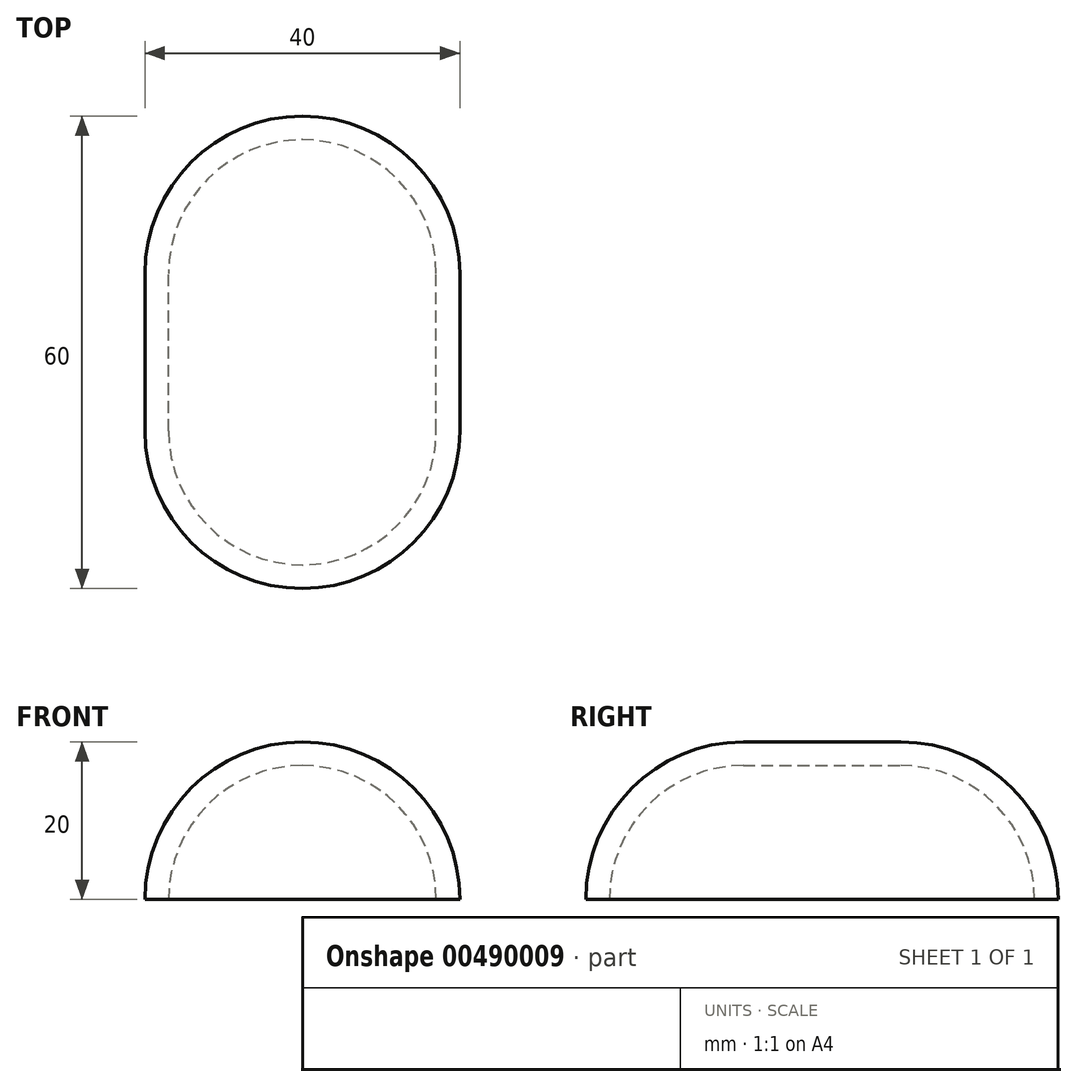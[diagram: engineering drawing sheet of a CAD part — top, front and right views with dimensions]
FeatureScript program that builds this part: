
annotation { "Feature Type Name" : "Feature", "Feature Type Description" : "" }
export const myFeature = defineFeature(function(context is Context, id is Id, definition is map)
    precondition{}
    {
        {
            var Q0;
            Q0=qCreatedBy(makeId("Top.planeOp"),FACE);
            var sketch = newSketch(context, id + "F0", { "sketchPlane" : qUnion([Q0])});
            skLineSegment(sketch, "E0.bottom", {"start": v(0, -30) * mm, "end": v(0, -30) * mm});
            skLineSegment(sketch, "E0.top", {"start": v(0, 30) * mm, "end": v(0, 30) * mm});
            skLineSegment(sketch, "E0.left", {"start": v(20, -10) * mm, "end": v(20, 10) * mm});
            skLineSegment(sketch, "E0.right", {"start": v(-20, -10) * mm, "end": v(-20, 10) * mm});
            skPoint(sketch, "E0.middle", {"position": v(0, 0) * mm});
            skPoint(sketch, "E1.visualSharp", {"position": v(-20, 30) * mm});
            skArc(sketch, "E1.filletArc", {"start": v(0, 30) * mm, "mid": v(-14.14, 24.14) * mm, "end": v(-20, 10) * mm});
            skPoint(sketch, "E2.visualSharp", {"position": v(20, 30) * mm});
            skArc(sketch, "E2.filletArc", {"start": v(20, 10) * mm, "mid": v(14.14, 24.14) * mm, "end": v(0, 30) * mm});
            skPoint(sketch, "E3.visualSharp", {"position": v(20, -30) * mm});
            skArc(sketch, "E3.filletArc", {"start": v(0, -30) * mm, "mid": v(14.14, -24.14) * mm, "end": v(20, -10) * mm});
            skPoint(sketch, "E4.visualSharp", {"position": v(-20, -30) * mm});
            skArc(sketch, "E4.filletArc", {"start": v(-20, -10) * mm, "mid": v(-14.14, -24.14) * mm, "end": v(0, -30) * mm});
            skSolve(sketch);
        }
        {
            var Q0;
            Q0=makeQuery(id+"F0.imprint","IMPRINT",FACE,{"disambiguationData":[TD([[makeQuery(id+"F0.imprint","IMPRINT",EDGE,{"derivedFrom":sQuery(id+"F0.wireOp",EDGE,"E0.left")}),1.0]])]});
            extrude(context, id + "F1", {"entities" : qUnion([Q0]), "depth" : 20 * mm});
        }
        {
            var Q0;
            Q0=makeQuery(id+"F1.opExtrude","CAP_EDGE",EDGE,{"disambiguationData":[OSD([sQuery(id+"F0.wireOp",EDGE,"E1.filletArc"),sQuery(id+"F0.wireOp",EDGE,"E2.filletArc")])],"isStart":false});
            fillet(context, id + "F2", {"entities" : qUnion([Q0]), "radius" : 20 * mm, "tangentPropagation" : true, "allowEdgeOverflow" : false});
        }
        {
            var Q0;
            Q0=makeQuery(id+"F1.opExtrude","CAP_FACE",FACE,{"disambiguationData":[OSD([sQuery(id+"F0.wireOp",EDGE,"E0.left"),sQuery(id+"F0.wireOp",EDGE,"E0.right"),sQuery(id+"F0.wireOp",EDGE,"E1.filletArc"),sQuery(id+"F0.wireOp",EDGE,"E2.filletArc"),sQuery(id+"F0.wireOp",EDGE,"E3.filletArc"),sQuery(id+"F0.wireOp",EDGE,"E4.filletArc")])],"isStart":true});
            shell(context, id + "F3", {"entities" : qUnion([Q0]), "thickness" : 3 * mm});
        }
    });
